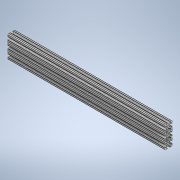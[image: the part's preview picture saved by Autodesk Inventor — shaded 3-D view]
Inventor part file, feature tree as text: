
AUTODESK INVENTOR PART (.ipt)
format: ipt  version: 2020 (Build 240168000, 168)  size: 378,368 bytes
history: native  units: in
note: dims shown in document units (in); Inventor stores cm internally (conversion verified against a paired STEP export)
features: sketch x2, extrude x1
ambient origin geometry x8: Origin, YZ Plane, XZ Plane, XY Plane, X Axis, Y Axis, Z Axis, Center Point
bodies: Solid1 (feature_tree)
feature tree (3):
  extrude  "Extrusion1"  [1 undecoded]
  sketch  "Sketch2"
  sketch  "Sketch1"  dims[d0=21.0in d1=0.0in]
note: 1 required parameter value undecoded (feature->parameter linkage not recoverable at this tier; creation-order binding heuristic only, values carry confidence <= 0.55)
